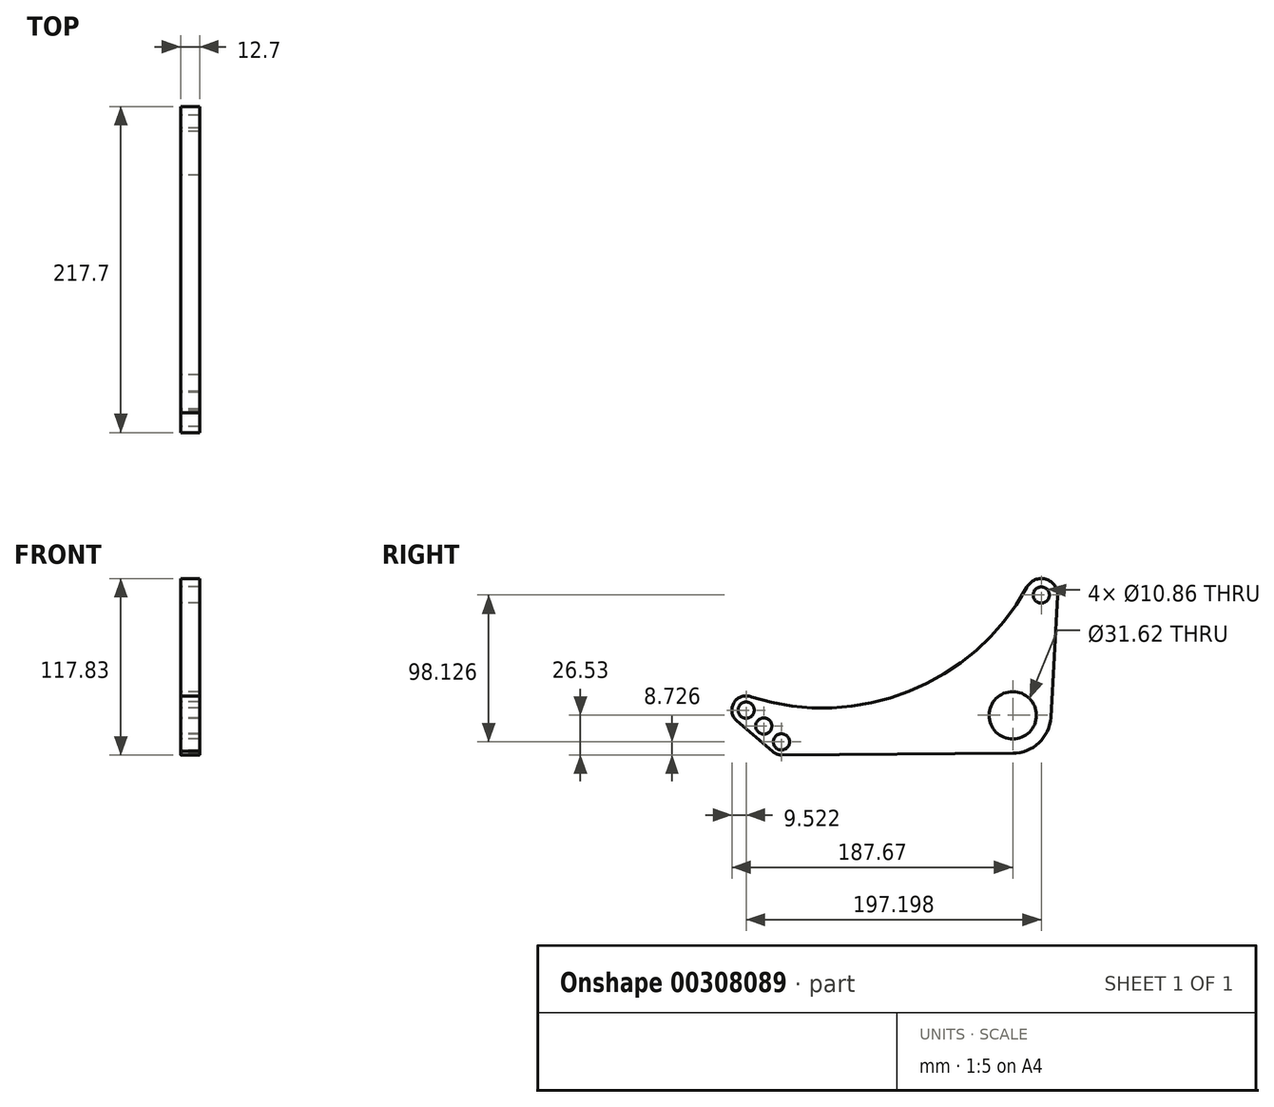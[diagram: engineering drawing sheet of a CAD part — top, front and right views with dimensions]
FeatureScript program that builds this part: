
annotation { "Feature Type Name" : "Feature", "Feature Type Description" : "" }
export const myFeature = defineFeature(function(context is Context, id is Id, definition is map)
    precondition{}
    {
        {
            var Q0;
            Q0=qCreatedBy(makeId("Right.planeOp"),FACE);
            var sketch = newSketch(context, id + "F0", { "sketchPlane" : qUnion([Q0])});
            skCircle(sketch, "E0", {"center": v(0, 0) * mm, "radius": 15.81 * mm});
            skArc(sketch, "E1", {"start": v(0, -25.4) * mm, "mid": v(17.44, -18.47) * mm, "end": v(25.36, -1.45) * mm});
            skCircle(sketch, "E2", {"center": v(-154.55, -17.8) * mm, "radius": 5.43 * mm});
            skLineSegment(sketch, "E3", {"start": v(-154.55, -17.8) * mm, "end": v(-178.15, 3.44) * mm, "construction": true});
            skCircle(sketch, "E4", {"center": v(-178.15, 3.44) * mm, "radius": 5.43 * mm});
            skCircle(sketch, "E5", {"center": v(-166.35, -7.18) * mm, "radius": 5.43 * mm});
            skCircle(sketch, "E6", {"center": v(19.05, 80.32) * mm, "radius": 5.43 * mm});
            skArc(sketch, "E7", {"start": v(30.01, 79.7) * mm, "mid": v(22.08, 90.87) * mm, "end": v(9.42, 85.6) * mm});
            skLineSegment(sketch, "E8", {"start": v(30.01, 79.7) * mm, "end": v(25.36, -1.45) * mm});
            skArc(sketch, "E9", {"start": v(-174.65, 12.28) * mm, "mid": v(-69.43, 15.85) * mm, "end": v(9.42, 85.6) * mm});
            skArc(sketch, "E10", {"start": v(-174.45, 12.22) * mm, "mid": v(-186.25, 8.45) * mm, "end": v(-184.34, -3.8) * mm});
            skArc(sketch, "E11", {"start": v(-160.69, -24.02) * mm, "mid": v(-157.84, -25.9) * mm, "end": v(-154.49, -26.53) * mm});
            skLineSegment(sketch, "E12", {"start": v(0, -25.4) * mm, "end": v(-154.74, -26.54) * mm});
            skLineSegment(sketch, "E13", {"start": v(-160.69, -24.02) * mm, "end": v(-184.34, -3.8) * mm});
            skSolve(sketch);
        }
        {
            var Q0;
            Q0=makeQuery(id+"F0.imprint","IMPRINT",FACE,{"disambiguationData":[TD([[makeQuery(id+"F0.imprint","IMPRINT",EDGE,{"derivedFrom":sQuery(id+"F0.wireOp",EDGE,"E0")}),-1.0]])]});
            extrude(context, id + "F1", {"entities" : qUnion([Q0]), "depth" : 12.7 * mm, "offsetDistance" : 25.4 * mm});
        }
    });
